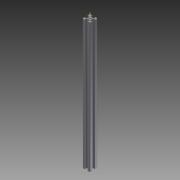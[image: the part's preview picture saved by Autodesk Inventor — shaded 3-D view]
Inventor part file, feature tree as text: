
AUTODESK INVENTOR PART (.ipt)
format: ipt  version: 2012 (Build 160160000, 160)  size: 210,944 bytes
history: native  units: mm
features: extrude x1, other x1, pattern_circular x1, sketch x1
ambient origin geometry x8: Origin, YZ Plane, XZ Plane, XY Plane, X Axis, Y Axis, Z Axis, Center Point
feature tree (4):
  extrude  "Extrusion2"  Depth=10.0mm
  other  "Work Axis5"
  pattern_circular  "Circular Pattern2"  [2 undecoded]
  sketch  "Sketch1"  dims[d0=10.0mm d1=10.0mm d3=1.4mm d4=6.1mm d5=6.1mm d6=3.1mm d7=3.1mm d8=2.5mm d9=5.7mm d10=5.7mm d12=2.0mm d14=2.5mm d15=3.2mm d21=1.2mm d22=0.5mm d23=0.5mm d24=0.5mm d25=0.5mm d26=0.2mm d27=0.2mm d28=0.2mm d29=0.2mm d30=350.0mm d31=0.0mm d32=40.0mm d33=360.0deg d48=0.1mm d67=4.0mm]
note: 2 required parameter values undecoded (feature->parameter linkage not recoverable at this tier; creation-order binding heuristic only, values carry confidence <= 0.55)
